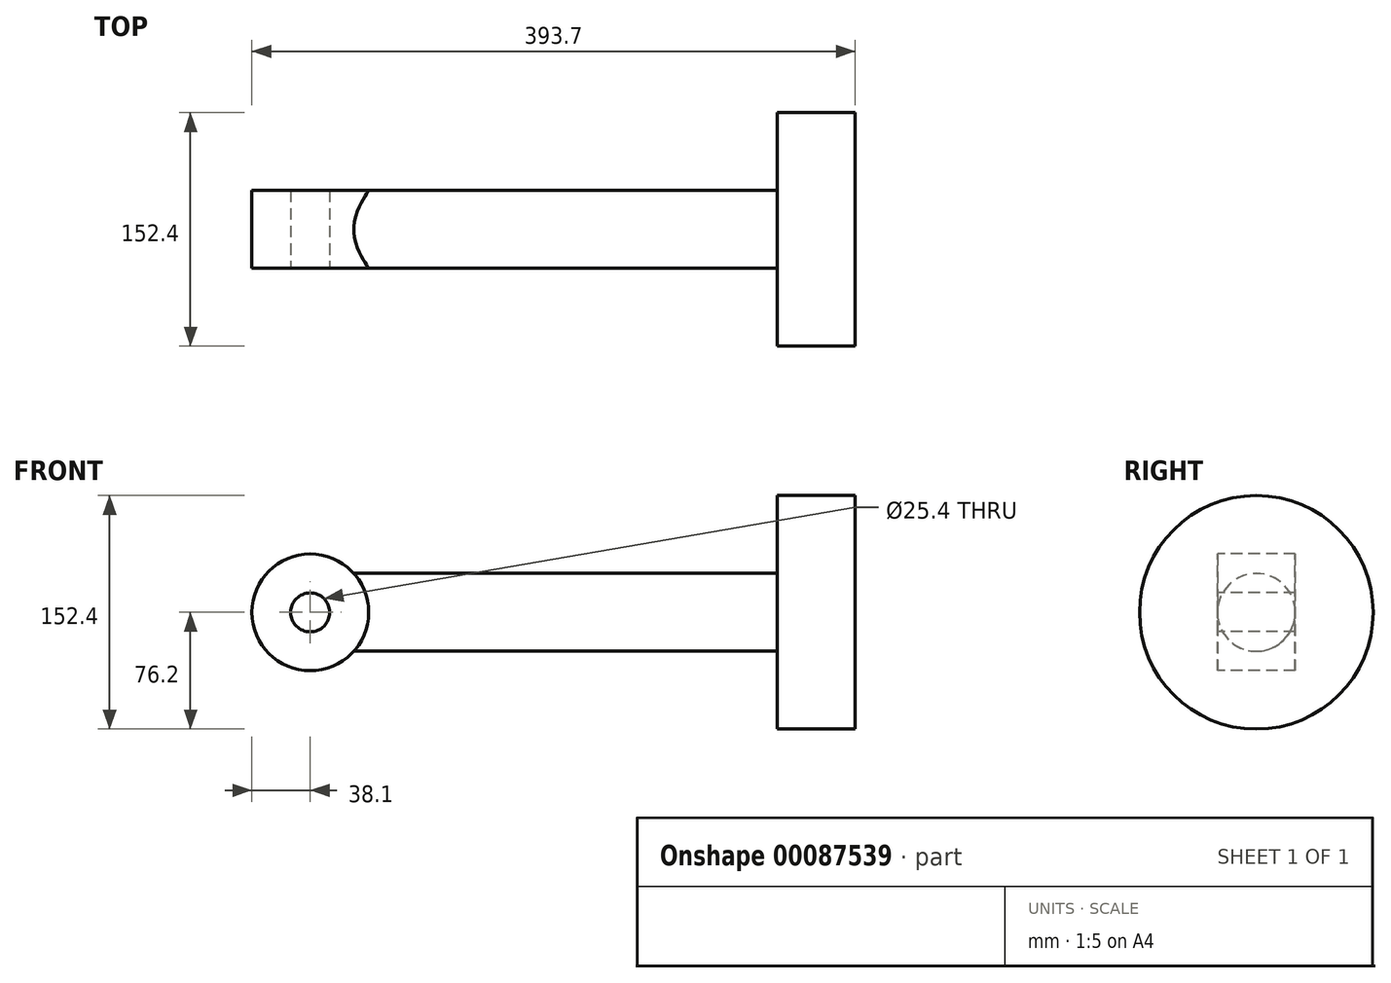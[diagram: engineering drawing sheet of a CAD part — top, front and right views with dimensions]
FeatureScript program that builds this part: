
annotation { "Feature Type Name" : "Feature", "Feature Type Description" : "" }
export const myFeature = defineFeature(function(context is Context, id is Id, definition is map)
    precondition{}
    {
        {
            var Q0;
            Q0=qCreatedBy(makeId("Front.planeOp"),FACE);
            var sketch = newSketch(context, id + "F0", { "sketchPlane" : qUnion([Q0])});
            skLineSegment(sketch, "E0", {"start": v(0, 0) * mm, "end": v(-355.6, 0) * mm});
            skLineSegment(sketch, "E1", {"start": v(-355.6, 0) * mm, "end": v(-355.6, 25.4) * mm});
            skLineSegment(sketch, "E2", {"start": v(-355.6, 25.4) * mm, "end": v(-50.8, 25.4) * mm});
            skLineSegment(sketch, "E3", {"start": v(-50.8, 25.4) * mm, "end": v(-50.8, 76.2) * mm});
            skLineSegment(sketch, "E4", {"start": v(-50.8, 76.2) * mm, "end": v(0, 76.2) * mm});
            skLineSegment(sketch, "E5", {"start": v(0, 76.2) * mm, "end": v(0, 0) * mm});
            skSolve(sketch);
        }
        {
            var Q0;
            Q0=makeQuery(id+"F0.imprint","IMPRINT",FACE,{"disambiguationData":[TD([[makeQuery(id+"F0.imprint","IMPRINT",EDGE,{"derivedFrom":sQuery(id+"F0.wireOp",EDGE,"E0")}),-1.0]])]});
            var Q1;
            Q1=sQuery(id+"F0.wireOp",EDGE,"E0");
            revolve(context, id + "F1", {"entities" : qUnion([Q0]), "axis" : qUnion([Q1]), "revolveType" : RevolveType.FULL});
        }
        {
            var Q0;
            Q0=makeQuery(id+"F1.opRevolve","SWEPT_FACE",FACE,{"disambiguationData":[OSD([sQuery(id+"F0.wireOp",EDGE,"E1")])]});
            var sketch = newSketch(context, id + "F2", { "sketchPlane" : qUnion([Q0])});
            skLineSegment(sketch, "E6", {"start": v(0, 0) * mm, "end": v(-25.4, 0) * mm, "construction": true});
            skLineSegment(sketch, "E7", {"start": v(-25.4, 0) * mm, "end": v(-25.4, 12.7) * mm, "construction": true});
            skLineSegment(sketch, "E8", {"start": v(-25.4, 12.7) * mm, "end": v(25.4, 12.7) * mm});
            skLineSegment(sketch, "E9", {"start": v(25.4, 12.7) * mm, "end": v(25.4, 38.1) * mm});
            skLineSegment(sketch, "E10", {"start": v(25.4, 38.1) * mm, "end": v(-25.4, 38.1) * mm});
            skLineSegment(sketch, "E11", {"start": v(-25.4, 38.1) * mm, "end": v(-25.4, 12.7) * mm});
            skLineSegment(sketch, "E12", {"start": v(25.4, 12.7) * mm, "end": v(25.4, 0) * mm, "construction": true});
            skSolve(sketch);
        }
        {
            var Q0;
            Q0 = qSketchRegion(id + "F2", true);
            var Q1;
            Q1=sQuery(id+"F2.wireOp",EDGE,"E6");
            revolve(context, id + "F3", {"operationType" : NewBodyOperationType.ADD, "entities" : qUnion([Q0]), "axis" : qUnion([Q1]), "revolveType" : RevolveType.FULL});
        }
        {
            var Q0;
            Q0=makeQuery(id+"F3.opRevolve","SWEPT_FACE",FACE,{"disambiguationData":[OSD([sQuery(id+"F2.wireOp",EDGE,"E9")])]});
            var sketch = newSketch(context, id + "F4", { "sketchPlane" : qUnion([Q0])});
            skCircle(sketch, "E13", {"center": v(-355.6, 0) * mm, "radius": 12.7 * mm});
            skSolve(sketch);
        }
        {
            var Q0;
            Q0=makeQuery(id+"F4.imprint","IMPRINT",FACE,{"disambiguationData":[TD([[makeQuery(id+"F4.imprint","IMPRINT",EDGE,{"derivedFrom":sQuery(id+"F4.wireOp",EDGE,"E13")}),1.0]])]});
            extrude(context, id + "F5", {"entities" : qUnion([Q0]), "operationType" : NewBodyOperationType.REMOVE, "oppositeDirection" : true, "depth" : 72.92 * mm});
        }
    });
